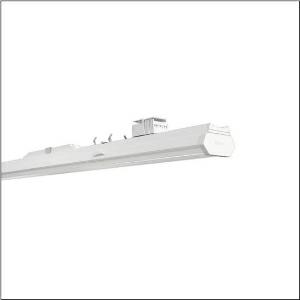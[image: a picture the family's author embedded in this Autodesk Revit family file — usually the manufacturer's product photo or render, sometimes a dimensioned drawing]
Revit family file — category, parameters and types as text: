
# Revit family: licross_r__21_protected_mo_52td12dn4a5gd_b3fc
name_source: partatom
category: Lighting Fixtures
units: mm (PartAtom-declared; Revit-internal decimal feet)

## family parameters
Cut with Voids When Loaded = No
Host = Face
Light Source = No
Part Type = Normal
Room Calculation Point = No
Round Connector Dimension = Use Diameter
Shared = No

## types (1)
- --- (1 x LED, 1610 lm, 10.2 W, 4000K)
    Apparent Load = 10 VA
    CIE Flux Codes = 73 92 98 99 100
    Color Rendering = 80
    Color Temperature = 4000K
    Default Elevation = 1800 mm
    Description = Licross® 21 Protected MO, luminaire insert, of sheet steel, galvanised, coil coated, white, length: 1.500mm, width: 90mm, height: 103mm, LED rated luminous flux: 10.700lm, light colour: 840, control gear: DALI 2 (for two DALI lines), with plug, 6-pole, with phase selection, mains connection: 220..240V, AC/DC, 0/50..60Hz, rated input power: 62W, without changeover relay, for emergency light function, for central battery installations according to DIN EN 60598-2-22, halogen-free wiring, primary light control with lens, of plastic, primary optical cover: cover, of PMMA, light emission: direct distribution, primary light characteristic: symmetric, protection rating (complete): IP54, insulation class (complete): insulation class I (protective earthing), certification: CE, ENEC, VDE, UKCA, protection symbol: D if used in an environment with non-conductive dust loads with corresponding accessories, impact resistance: IK06, permissible ambient temperature for indoor applications: -25..+35°C, standard: EN 60598-2-22, corresponds to IFS (International Featured Standards) requirements for safety and quality in the food industry, reducing of maximum allowable ambient temperature of 5°C with ceiling mounting, LABS conformity tested according to VDMA 24364:2018-05, packaging unit: 1 piece
    Height = 92 mm
    Lamp = 1 x LED
    Lamp Light Flux = 1610 lm
    Lamp Power = 10.2 W
    Lamp count = 1
    Length = 1500 mm
    Luminous efficacy = 158 lm/W
    Manufacturer = Siteco
    ModVariant = No
    Model = 52TD12DN4A5GD
    Mounting Place = Ceiling
    Mounting Type = Pendant
    Number of Poles = 1
    OnlyDefault = Yes
    Power Factor = 1
    Product Name = Licross® 21 Protected MO
    Product group = luminaire insert
    ProductGroupID = 902
    Protection Class = Protection class I
    Protection Degree = IP 54
    RLX_Detail_Level = 1
    RLX_Emergency_Light_Flux = 0 lm
    RLX_Emergency_Type = 0
    RLX_Emergency_Type_DB = No
    RlxData = <blob elided: 24797 chars, md5=87c3a623>
    Socket = socket
    Standby Power = 0 W
    System Light Flux = 1610 lm
    System Power = 10 W
    Type Comments = : DC mode (central or group accumulator) initial emergency light level
    Type Image = l_1256148.jpg
    URL = http://relux.com
    VarID = @adj_116260
    Voltage = 0 V
    Weight = 0.00 kg
    Width = 88 mm

## geometry (parser evidence)
native form markers: Blend x4, Sweep x10
no freeform markers — native parametric forms only
